# Revit family: Sanitary_Bidets_Sanindusa_Metal-Support-For-Wall-Mounted-Bidet
name_source: partatom
category: Plumbing Fixtures
revit_build: Autodesk Revit 2018 (Build: 20170223_1515(x64)
units: mm (PartAtom-declared; Revit-internal decimal feet)

## family parameters
Always vertical = Yes
Cut with Voids When Loaded = No
Host = Wall
OmniClass Number = 23.45.00.00
OmniClass Title = Sanitary, Laundry, and Cleaning Equipment
Part Type = Normal
Room Calculation Point = No
Round Connector Dimension = Use Diameter
Shared = No

## types (1)
- Sanindusa
    AssetType = Fixed
    Constituents = Supporting frame for mounting; Height adjustable galvanized support legs; Depth adjustable galvanised brackets for pre-wall installation; Two threaded rods with M10 nuts for attaching bidet; Height adjustable PE drain elbow ø 50 mm; Rubber sink trap seal, ø 32 mm; Other parts necessary to fix and connect the product.
Supporting frame for mounting; Height adjustable galvanized support legs; Depth adjustable galvanised brackets for pre-wall installation; Two threaded rods with M10 nuts for attaching bidet; Height adjustable PE drain elbow ø 50 mm; Rubber sink trap seal, ø 32 mm; Other parts necessary to fix and connect the product.
Supporting frame for mounting; Height adjustable galvanized support legs; Depth adjustable galvanised brackets for pre-wall installation; Two threaded rods with M10 nuts for attaching bidet; Height adjustable PE drain elbow ø 50 mm; Rubber sink trap seal, ø 32 mm; Other parts necessary to fix and connect the product.
    Cost = 0 $
    D = 355 mm
    Description = support for wall mounted bidet
    Edition number = 1
    Features = Supporting frame for wall-mounted bidet with an axial distance of 18 or 23 cm. For universal installation into solid walls.
    Finish = blue powder coating
    Installation Instructions = https://www.tec.SANINDUSA.pt
    Manufacturer = www.sanindusa.pt
    ManufacturerName = Sanindusa
    ManufacturerURL = www.tec.sanindusa.pt
    Material = Supporting frame made from 40 × 40 mm profiles with surface protected by blue powder coating
    ModelNumber = 430
    ModelReference = Components
    Name = Metal support for wall mounted bidet
    NominalHeight = 355 mm
    NominalLength = 460 mm
    NominalWidth = 85 mm
    Product Guid = 93dbdc16-85cf-4965-87bf-1b8f340f5aee
    Product data url = https://bimobject.com
    ProductInformation = https://www.tec.sanindusa.pt
    Size = 46x9x32
    URL = www.tec.sanindusa.pt
    Uniclass2015Code = Pr_40_20_93_62
    Uniclass2015Title = Pre-plumbed installation frames
    Uniclass2015Version = Products v1.6
    Version = 2
    WarrantyDescription = https://www.tec.sanindusa.pt
    WarrantyDurationParts = 5
    WarrantyDurationUnit = year
    WarrantyStartDate = 1900-12-31T23:59:59
    Weight = 6.00 kg

## geometry (parser evidence)
native form markers: Sweep x6
no freeform markers — native parametric forms only
